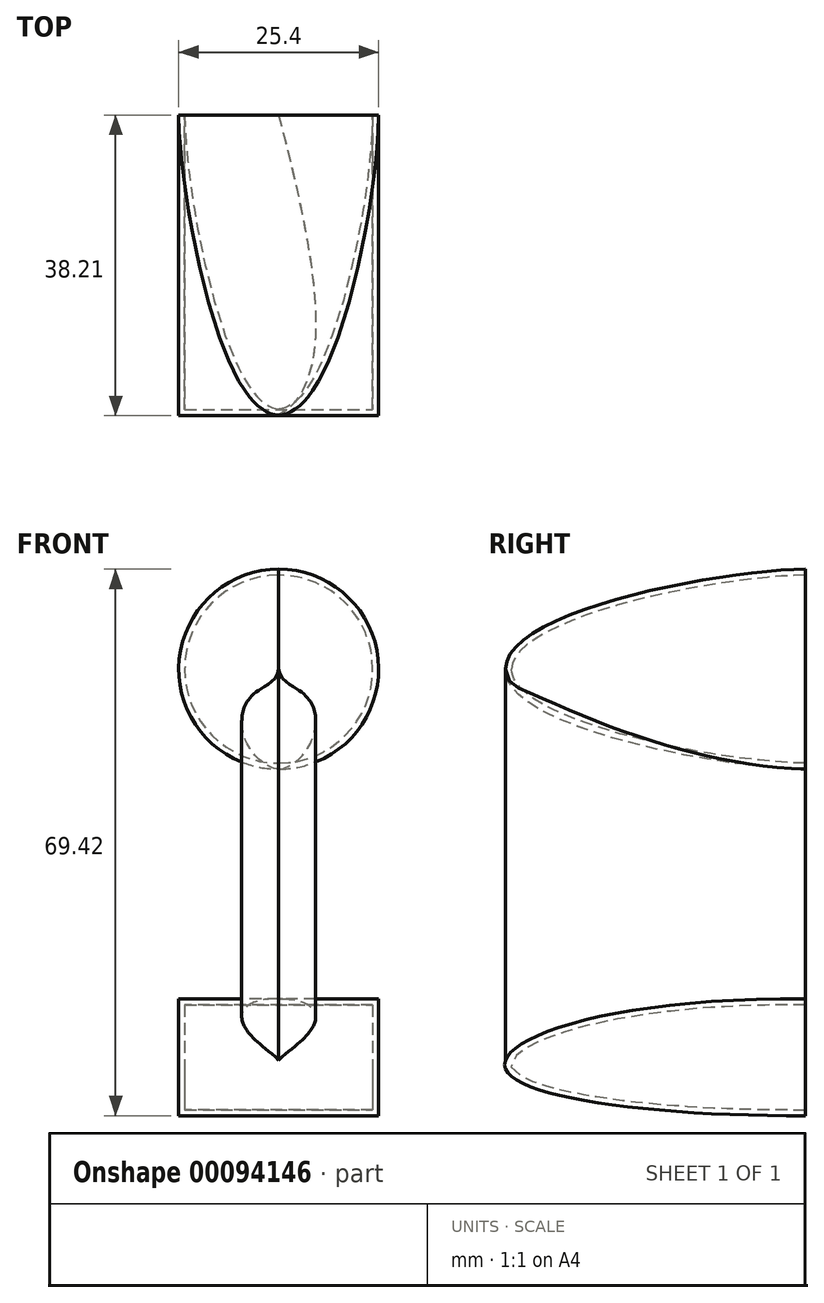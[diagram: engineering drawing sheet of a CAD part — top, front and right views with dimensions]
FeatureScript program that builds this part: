
annotation { "Feature Type Name" : "Feature", "Feature Type Description" : "" }
export const myFeature = defineFeature(function(context is Context, id is Id, definition is map)
    precondition{}
    {
        {
            var Q0;
            Q0=qCreatedBy(makeId("Right.planeOp"),FACE);
            var sketch = newSketch(context, id + "F0", { "sketchPlane" : qUnion([Q0])});
            skLineSegment(sketch, "E0", {"start": v(0, 0) * mm, "end": v(0, 50.8) * mm});
            skLineSegment(sketch, "E1", {"start": v(0, 0) * mm, "end": v(38.1, 0) * mm});
            skLineSegment(sketch, "E2", {"start": v(0, 50.8) * mm, "end": v(38.1, 50.8) * mm});
            skLineSegment(sketch, "E3", {"start": v(38.1, 50.8) * mm, "end": v(38.1, 63.5) * mm});
            skFitSpline(sketch, "E4", {"points": [v(38.1, 63.5) * mm, v(0, 50.8) * mm], "startDerivative": vector(-31.54, -0.26) * mm, "endDerivative": vector(0, -22.7) * mm});
            skSolve(sketch);
        }
        {
            var Q0;
            Q0=makeQuery(id+"F0.imprint","IMPRINT",FACE,{"disambiguationData":[TD([[makeQuery(id+"F0.imprint","IMPRINT",EDGE,{"derivedFrom":sQuery(id+"F0.wireOp",EDGE,"E2")}),1.0]])]});
            var Q1;
            Q1=sQuery(id+"F0.wireOp",EDGE,"E2");
            revolve(context, id + "F1", {"entities" : qUnion([Q0]), "axis" : qUnion([Q1]), "revolveType" : RevolveType.FULL});
        }
        {
            var Q0;
            Q0=makeQuery(id+"F1.opRevolve","SWEPT_FACE",FACE,{"disambiguationData":[OSD([sQuery(id+"F0.wireOp",EDGE,"E3")])]});
            shell(context, id + "F2", {"entities" : qUnion([Q0]), "thickness" : 0.76 * mm});
        }
        {
            var Q0;
            Q0=qCreatedBy(makeId("Right.planeOp"),FACE);
            var sketch = newSketch(context, id + "F3", { "sketchPlane" : qUnion([Q0])});
            skLineSegment(sketch, "E5", {"start": v(0, 0) * mm, "end": v(38.1, 0) * mm});
            skFitSpline(sketch, "E6", {"points": [v(38.1, 8.9) * mm, v(0, 0) * mm, v(38.1, -5.92) * mm], "startDerivative": vector(-147.66, 1.85) * mm, "endDerivative": vector(112.66, 0.63) * mm});
            skLineSegment(sketch, "E7", {"start": v(38.1, 8.9) * mm, "end": v(38.1, -5.92) * mm});
            skSolve(sketch);
        }
        {
            var Q0;
            Q0 = qSketchRegion(id + "F3", true);
            extrude(context, id + "F4", {"entities" : qUnion([Q0]), "depth" : 12.7 * mm, "hasSecondDirection" : true, "secondDirectionOppositeDirection" : true, "secondDirectionDepth" : 12.7 * mm});
        }
        {
            var Q0;
            Q0=makeQuery(id+"F4.opExtrude","SWEPT_FACE",FACE,{"disambiguationData":[OSD([sQuery(id+"F3.wireOp",EDGE,"E7")])]});
            shell(context, id + "F5", {"entities" : qUnion([Q0]), "thickness" : 0.76 * mm});
        }
        {
            var Q0;
            Q0=qCreatedBy(makeId("Top.planeOp"),FACE);
            cPlane(context, id + "F6", {"entities" : qUnion([Q0]), "cplaneType" : CPlaneType.OFFSET, "offset" : 12.7 * mm, "width" : 152.4 * mm, "height" : 152.4 * mm});
        }
        {
            var Q0;
            Q0=qCreatedBy(id+"F6.planeOp",FACE);
            var sketch = newSketch(context, id + "F7", { "sketchPlane" : qUnion([Q0])});
            skLineSegment(sketch, "E8", {"start": v(0, 0) * mm, "end": v(0, 38.1) * mm});
            skFitSpline(sketch, "E9", {"points": [v(0, 0) * mm, v(4.6, 9.13) * mm, v(0, 38.1) * mm], "startDerivative": vector(22.82, 10.97) * mm, "endDerivative": vector(-13.5, 52.83) * mm});
            skFitSpline(sketch, "E10.MirrorCS", {"points": [v(0, 0) * mm, v(-4.6, 9.13) * mm, v(0, 38.1) * mm], "startDerivative": vector(-22.82, 10.97) * mm, "endDerivative": vector(13.5, 52.83) * mm});
            skSolve(sketch);
        }
        {
            var Q0;
            Q0=makeQuery(id+"F7.imprint","IMPRINT",FACE,{"disambiguationData":[TD([[makeQuery(id+"F7.imprint","IMPRINT",EDGE,{"derivedFrom":sQuery(id+"F7.wireOp",EDGE,"E8")}),1.0]])]});
            var Q1;
            Q1=makeQuery(id+"F7.imprint","IMPRINT",FACE,{"disambiguationData":[TD([[makeQuery(id+"F7.imprint","IMPRINT",EDGE,{"derivedFrom":sQuery(id+"F7.wireOp",EDGE,"E8")}),-1.0]])]});
            extrude(context, id + "F8", {"entities" : qUnion([Q0, Q1]), "endBound" : BoundingType.UP_TO_NEXT, "depth" : 25.4 * mm, "hasSecondDirection" : true, "secondDirectionBound" : SecondDirectionBoundingType.UP_TO_NEXT, "secondDirectionOppositeDirection" : true, "secondDirectionDepth" : 25.4 * mm});
        }
    });
